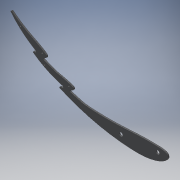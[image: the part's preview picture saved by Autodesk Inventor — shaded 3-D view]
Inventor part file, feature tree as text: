
AUTODESK INVENTOR PART (.ipt)
format: ipt  version: 2018 (Build 220112000, 112)  size: 201,728 bytes
history: native  units: mm
features: projected_geometry x3, extrude x2, sketch x2, fillet x1
ambient origin geometry x8: Origin, YZ Plane, XZ Plane, XY Plane, X Axis, Y Axis, Z Axis, Center Point
bodies: Body1 (feature_tree)
feature tree (8):
  extrude  "押し出し2"  Depth=4.0mm TaperAngle=0.0deg
  fillet  "フィレット2"  Radius=3.0mm
  extrude  "押し出し3"  Depth=100.0mm
  sketch  "スケッチ2"
  projected_geometry  "投影ループ4"
  projected_geometry  "投影ループ5"
  projected_geometry  "投影ループ6"
  sketch  "スケッチ3"
